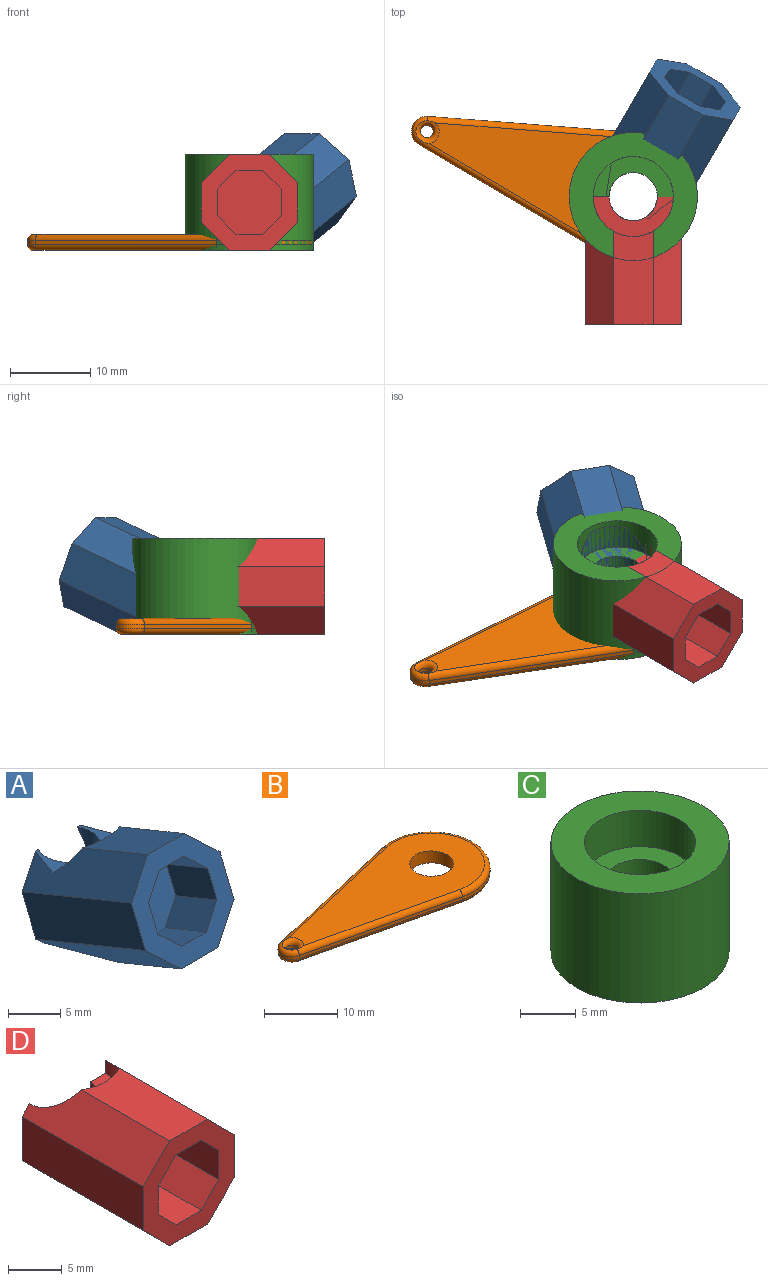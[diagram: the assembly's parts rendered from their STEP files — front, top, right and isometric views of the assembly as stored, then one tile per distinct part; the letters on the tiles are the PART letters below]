
ASSEMBLY  parts=4 mates=3
PART A: 24 faces, bbox 12x19.1x14.6 mm
  f0: plane 8x3.61mm, normal (0,0.93,-0.38), area 22.7mm2, adj f1,f8,f17,f20,f22,f23
  f1: plane 15.93x9.32mm, normal (0.71,0.27,0.65), area 68.5mm2, adj f0,f4,f17,f18,f21,f22
  f2: plane 15.93x9.32mm, normal (-0.71,0.27,0.65), area 68.5mm2, adj f3,f4,f5,f18,f21,f22
  f3: plane 8x3.61mm, normal (0,0.93,-0.38), area 22.7mm2, adj f2,f5,f6,f20,f22,f23
  f4: plane 8.79x4.97mm, normal (0,0.38,0.93), area 44.8mm2, adj f1,f2,f18,f21
  f5: plane 16.69x10.67mm, normal (-1,0,0), area 79.5mm2, adj f2,f3,f6,f18
  f6: plane 16.14x6.74mm, normal (-0.71,-0.27,-0.65), area 66.1mm2, adj f3,f5,f7,f18,f23
  f7: plane 8.5x4.97mm, normal (0,-0.38,-0.93), area 45.6mm2, adj f6,f8,f18,f23
  f8: plane 16.14x6.74mm, normal (0.71,-0.27,-0.65), area 66.1mm2, adj f0,f7,f17,f18,f23
  f9: plane 5.55x3.31mm, normal (0,-0.38,-0.93), area 19.9mm2, adj f10,f16,f18,f19
  f10: plane 6.44x4.44mm, normal (-0.71,-0.27,-0.65), area 19.9mm2, adj f9,f11,f18,f19
  f11: plane 6.81x5.34mm, normal (-1,0,0), area 19.9mm2, adj f10,f12,f18,f19
  f12: plane 6.44x4.44mm, normal (-0.71,0.27,0.65), area 19.9mm2, adj f11,f13,f18,f19
  f13: plane 5.55x3.31mm, normal (0,0.38,0.93), area 19.9mm2, adj f12,f14,f18,f19
  f14: plane 6.44x4.44mm, normal (0.71,0.27,0.65), area 19.9mm2, adj f13,f15,f18,f19
  f15: plane 6.81x5.34mm, normal (1,0,0), area 19.9mm2, adj f14,f16,f18,f19
  f16: plane 6.44x4.44mm, normal (0.71,-0.27,-0.65), area 19.9mm2, adj f9,f15,f18,f19
  f17: plane 16.69x10.67mm, normal (1,0,0), area 79.5mm2, adj f0,f1,f8,f18
  f18: plane 12x11.1mm, normal (0,-0.93,0.38), area 66.3mm2, adj f1,f2,f4,f5,f6,f7,f8,f9
  f19: plane 8x7.4mm, normal (0,-0.93,0.38), area 53mm2, adj f9,f10,f11,f12,f13,f14,f15,f16
  f20: cylinder r=3mm len=8mm, axis (0,0,1), area 72.5mm2, adj f0,f3,f22,f23
  f21: cylinder r=5mm len=8.92mm, axis (0,0,-1), area 24.7mm2, adj f1,f2,f4,f22
  f22: plane 8.92x6.47mm, normal (0,0,1), area 22.8mm2, adj f0,f1,f2,f3,f20,f21
  f23: plane 10.56x7.37mm, normal (0,0,-1), area 53.3mm2, adj f0,f3,f6,f7,f8,f20
PART B: 18 faces, bbox 37.9x17.3x2 mm
  f0: plane 25.62x5.94mm, normal (-0.23,0.97,0), area 13.2mm2, adj f1,f5,f11,f16
  f1: cylinder r=1.9mm len=3.7mm, axis (0,0,1), area 2.6mm2, adj f0,f2,f9,f13
  f2: plane 25.62x5.94mm, normal (-0.23,-0.97,0), area 13.2mm2, adj f1,f5,f10,f15
  f3: cylinder r=0.8mm len=1.6mm, axis (0,0,1), area 2.5mm2, adj f8,f14
  f4: cylinder r=3mm len=6mm, axis (0,0,1), area 37.7mm2, adj f6,f7
  f5: cylinder r=8mm len=16mm, axis (0,0,1), area 14.4mm2, adj f0,f2,f12,f17
  f6: plane 33.5x14.5mm, normal (0,0,-1), area 283.5mm2, adj f4,f14,f15,f16,f17
  f7: plane 33.5x14.5mm, normal (0,0,1), area 283.5mm2, adj f4,f8,f10,f11,f12
  f8: torus R=1.55mm, axis (0,0,1), area 6.9mm2, adj f3,f7,f9,f10,f11
  f9: torus R=1.15mm, axis (0,0,1), area 4.5mm2, adj f1,f8,f10,f11
  f10: cylinder r=0.75mm len=25.79mm, axis (0.97,-0.23,0), area 30.9mm2, adj f2,f7,f8,f9,f12
  f11: cylinder r=0.75mm len=25.79mm, axis (-0.97,-0.23,0), area 30.9mm2, adj f0,f7,f8,f9,f12
  f12: torus R=7.25mm, axis (0,0,1), area 32.7mm2, adj f5,f7,f10,f11
  f13: torus R=1.15mm, axis (0,0,1), area 4.5mm2, adj f1,f14,f15,f16
  f14: torus R=1.55mm, axis (0,0,1), area 6.9mm2, adj f3,f6,f13,f15,f16
  f15: cylinder r=0.75mm len=25.79mm, axis (-0.97,0.23,0), area 30.9mm2, adj f2,f6,f13,f14,f17
  f16: cylinder r=0.75mm len=25.79mm, axis (0.97,0.23,0), area 30.9mm2, adj f0,f6,f13,f14,f17
  f17: torus R=7.25mm, axis (0,0,1), area 32.7mm2, adj f5,f6,f15,f16
PART C: 6 faces, bbox 16x16x12 mm
  f0: cylinder r=3mm len=8mm, axis (0,0,1), area 150.8mm2, adj f3,f5
  f1: cylinder r=8mm len=16mm, axis (0,0,-1), area 603.2mm2, adj f2,f3
  f2: plane 16x16mm, normal (0,0,1), area 122.5mm2, adj f1,f4
  f3: plane 16x16mm, normal (0,0,-1), area 172.8mm2, adj f0,f1
  f4: cylinder r=5mm len=10mm, axis (0,0,-1), area 125.7mm2, adj f2,f5
  f5: plane 10x10mm, normal (0,0,1), area 50.3mm2, adj f0,f4
PART D: 23 faces, bbox 12x16x12 mm
  f0: plane 8.97x3mm, normal (0,1,0), area 18.9mm2, adj f3,f8,f17,f20,f21,f22
  f1: plane 8.97x3mm, normal (0,1,0), area 18.9mm2, adj f4,f5,f6,f20,f21,f22
  f2: plane 11.66x4.97mm, normal (0,0,1), area 55.7mm2, adj f3,f4,f18,f21
  f3: plane 16x3.51mm, normal (0.71,0,0.71), area 68.6mm2, adj f0,f2,f17,f18,f21
  f4: plane 16x3.51mm, normal (-0.71,0,0.71), area 68.6mm2, adj f1,f2,f5,f18,f21
  f5: plane 16x4.97mm, normal (-1,0,0), area 79.5mm2, adj f1,f4,f6,f18
  f6: plane 16x3.51mm, normal (-0.71,0,-0.71), area 78.7mm2, adj f1,f5,f7,f18,f20
  f7: plane 14.32x4.97mm, normal (0,0,-1), area 66.6mm2, adj f6,f8,f18,f20
  f8: plane 16x3.51mm, normal (0.71,0,-0.71), area 78.7mm2, adj f0,f7,f17,f18,f20
  f9: plane 6x3.31mm, normal (0,0,-1), area 19.9mm2, adj f10,f16,f18,f19
  f10: plane 6x2.34mm, normal (-0.71,0,-0.71), area 19.9mm2, adj f9,f11,f18,f19
  f11: plane 6x3.31mm, normal (-1,0,0), area 19.9mm2, adj f10,f12,f18,f19
  f12: plane 6x2.34mm, normal (-0.71,0,0.71), area 19.9mm2, adj f11,f13,f18,f19
  f13: plane 6x3.31mm, normal (0,0,1), area 19.9mm2, adj f12,f14,f18,f19
  f14: plane 6x2.34mm, normal (0.71,0,0.71), area 19.9mm2, adj f13,f15,f18,f19
  f15: plane 6x3.31mm, normal (1,0,0), area 19.9mm2, adj f14,f16,f18,f19
  f16: plane 6x2.34mm, normal (0.71,0,-0.71), area 19.9mm2, adj f9,f15,f18,f19
  f17: plane 16x4.97mm, normal (1,0,0), area 79.5mm2, adj f0,f3,f8,f18
  f18: plane 12x12mm, normal (0,-1,0), area 66.3mm2, adj f2,f3,f4,f5,f6,f7,f8,f9
  f19: plane 8x8mm, normal (0,-1,0), area 53mm2, adj f9,f10,f11,f12,f13,f14,f15,f16
  f20: cylinder r=3mm len=8mm, axis (0,0,1), area 74.2mm2, adj f0,f1,f6,f7,f8,f22
  f21: cylinder r=5mm len=10mm, axis (0,0,-1), area 45.6mm2, adj f0,f1,f2,f3,f4,f22
  f22: plane 10x5mm, normal (0,0,1), area 25.1mm2, adj f0,f1,f20,f21
PLACE A rot(axis=(0,0,1),150deg) t=(0,0,0)mm
PLACE B rot(axis=(0,0,-1),17.5deg) t=(0,0,0)mm
PLACE C rot(axis=(1,0,0),0deg) t=(0,0,0)mm fixed
PLACE D at identity
MATE revolute C.f1 <-> A.f21  axis (0,0,-1) through (0,0,-6)mm
MATE fastened C.f1 <-> D.f21  axis (0,0,-1) through (0,0,-6)mm
MATE revolute C.f1 <-> B.f5  axis (0,0,-1) through (0,0,-6)mm
